# Revit family: HERZ Metering Station 4000
name_source: partatom
category: Rohrzubehör
units: mm (PartAtom-declared; Revit-internal decimal feet)

## family parameters
Arbeitsebenenbasiert = Nein
Beim Laden mit Abzugskörper schneiden = Nein
Bemaßung runder Anschluss = Durchmesser verwenden
Gemeinsam genutzt = Nein
Immer vertikal = Ja
OmniClass-Nummer = 23.65.55.14
OmniClass-Titel = Valves for Liquid Services
Teiletyp = Unterbricht

## types (1)
- HERZ Metering Station 4000
    Application = HERZ metering stations are installed in the circuit of water heating and cooling systems and enable the hydraulic balancing of the circuits with one another.
The metering stations can be used in the supply line as well as in the return line.
They are either installed closely connected to a HERZ commissioning valve to form a complete set or used in connection with a HERZ shutoff valve.
The circuit is adjusted by setting the commissioning valve while measuring the pressure loss on the metering station.
    Body = brass, CC770S
    Hersteller = HERZ Armaturen Ges.m.b.H.
    Max. operating pressure = 2000000.0 Pa
    Max. operating temperature (from DN40) = 110 °C
    Max. operating temperature (until DN32) = 130 °C
    Medium = Water purity in accordance with the OeNORM H5195 and VDI 2035 standards.
Ethylene and propylene glycol can be mixed to a ratio of 25 - 50 vol. %.
    Min. operating temperature = -20 °C
    Model = The metering station made of DZR brass has two measuring valves.
According to EN 10226, the inlet has an internal thread Rp and the outlet an external thread R.
    S03 = 10 mm  [stored 0.0328084 ft]
    SCRNCODE = 02;01;02
    SCRNSEQ = AWI;AWI_TYP="1001";02
    Test point = brass, CW602N
    URL = www.herzvalves.com
    Vorgabe-Ansicht = 0 mm  [stored 0 ft]

note: [stored X ft] marks values corroborated as IEEE doubles in the binary element streams (Revit-internal decimal feet)
